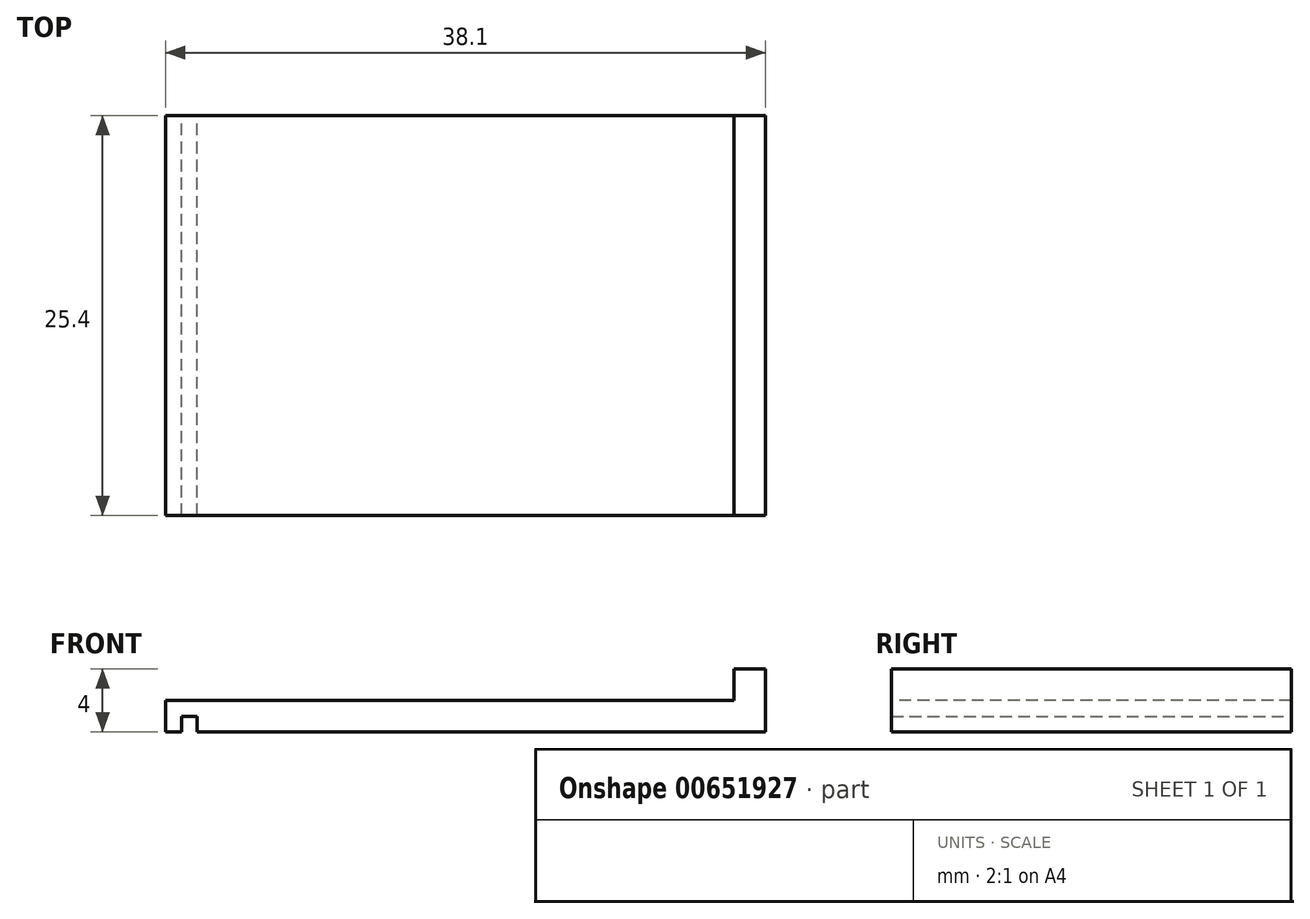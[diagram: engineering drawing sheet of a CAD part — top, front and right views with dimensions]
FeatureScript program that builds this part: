
annotation { "Feature Type Name" : "Feature", "Feature Type Description" : "" }
export const myFeature = defineFeature(function(context is Context, id is Id, definition is map)
    precondition{}
    {
        {
            var Q0;
            Q0=qCreatedBy(makeId("Top.planeOp"),FACE);
            var sketch = newSketch(context, id + "F0", { "sketchPlane" : qUnion([Q0])});
            skLineSegment(sketch, "E0.bottom", {"start": v(-17.7, 11.97) * mm, "end": v(20.4, 11.97) * mm});
            skLineSegment(sketch, "E0.top", {"start": v(-17.7, -13.43) * mm, "end": v(20.4, -13.43) * mm});
            skLineSegment(sketch, "E0.left", {"start": v(-17.7, 11.97) * mm, "end": v(-17.7, -13.43) * mm});
            skLineSegment(sketch, "E0.right", {"start": v(20.4, 11.97) * mm, "end": v(20.4, -13.43) * mm});
            skSolve(sketch);
        }
        {
            var Q0;
            Q0 = qSketchRegion(id + "F0", true);
            extrude(context, id + "F1", {"entities" : qUnion([Q0]), "depth" : 2 * mm, "offsetDistance" : 25.4 * mm});
        }
        {
            var Q0;
            Q0=makeQuery(id+"F1.opExtrude","CAP_FACE",FACE,{"disambiguationData":[OSD([sQuery(id+"F0.wireOp",EDGE,"E0.bottom"),sQuery(id+"F0.wireOp",EDGE,"E0.top"),sQuery(id+"F0.wireOp",EDGE,"E0.left"),sQuery(id+"F0.wireOp",EDGE,"E0.right")])],"isStart":false});
            var sketch = newSketch(context, id + "F2", { "sketchPlane" : qUnion([Q0])});
            skLineSegment(sketch, "E1.bottom", {"start": v(20.4, 11.97) * mm, "end": v(18.4, 11.97) * mm});
            skLineSegment(sketch, "E1.top", {"start": v(20.4, -13.43) * mm, "end": v(18.4, -13.43) * mm});
            skLineSegment(sketch, "E1.left", {"start": v(20.4, 11.97) * mm, "end": v(20.4, -13.43) * mm});
            skLineSegment(sketch, "E1.right", {"start": v(18.4, 11.97) * mm, "end": v(18.4, -13.43) * mm});
            skSolve(sketch);
        }
        {
            var Q0;
            Q0 = qSketchRegion(id + "F2", true);
            extrude(context, id + "F3", {"entities" : qUnion([Q0]), "operationType" : NewBodyOperationType.ADD, "depth" : 2 * mm, "offsetDistance" : 25.4 * mm});
        }
        {
            var Q0;
            Q0=makeQuery(id+"F1.opExtrude","CAP_FACE",FACE,{"disambiguationData":[OSD([sQuery(id+"F0.wireOp",EDGE,"E0.bottom"),sQuery(id+"F0.wireOp",EDGE,"E0.top"),sQuery(id+"F0.wireOp",EDGE,"E0.left"),sQuery(id+"F0.wireOp",EDGE,"E0.right")])],"isStart":true});
            var sketch = newSketch(context, id + "F4", { "sketchPlane" : qUnion([Q0])});
            skLineSegment(sketch, "E2.right", {"start": v(-16.7, 13.43) * mm, "end": v(-16.7, -11.97) * mm});
            skLineSegment(sketch, "E3.bottom", {"start": v(-16.7, 13.43) * mm, "end": v(-15.7, 13.43) * mm});
            skLineSegment(sketch, "E3.top", {"start": v(-16.7, -11.97) * mm, "end": v(-15.7, -11.97) * mm});
            skLineSegment(sketch, "E3.right", {"start": v(-15.7, 13.43) * mm, "end": v(-15.7, -11.97) * mm});
            skSolve(sketch);
        }
        {
            var Q0;
            Q0 = qSketchRegion(id + "F4", true);
            extrude(context, id + "F5", {"entities" : qUnion([Q0]), "operationType" : NewBodyOperationType.REMOVE, "oppositeDirection" : true, "depth" : 1 * mm, "offsetDistance" : 25.4 * mm});
        }
    });
